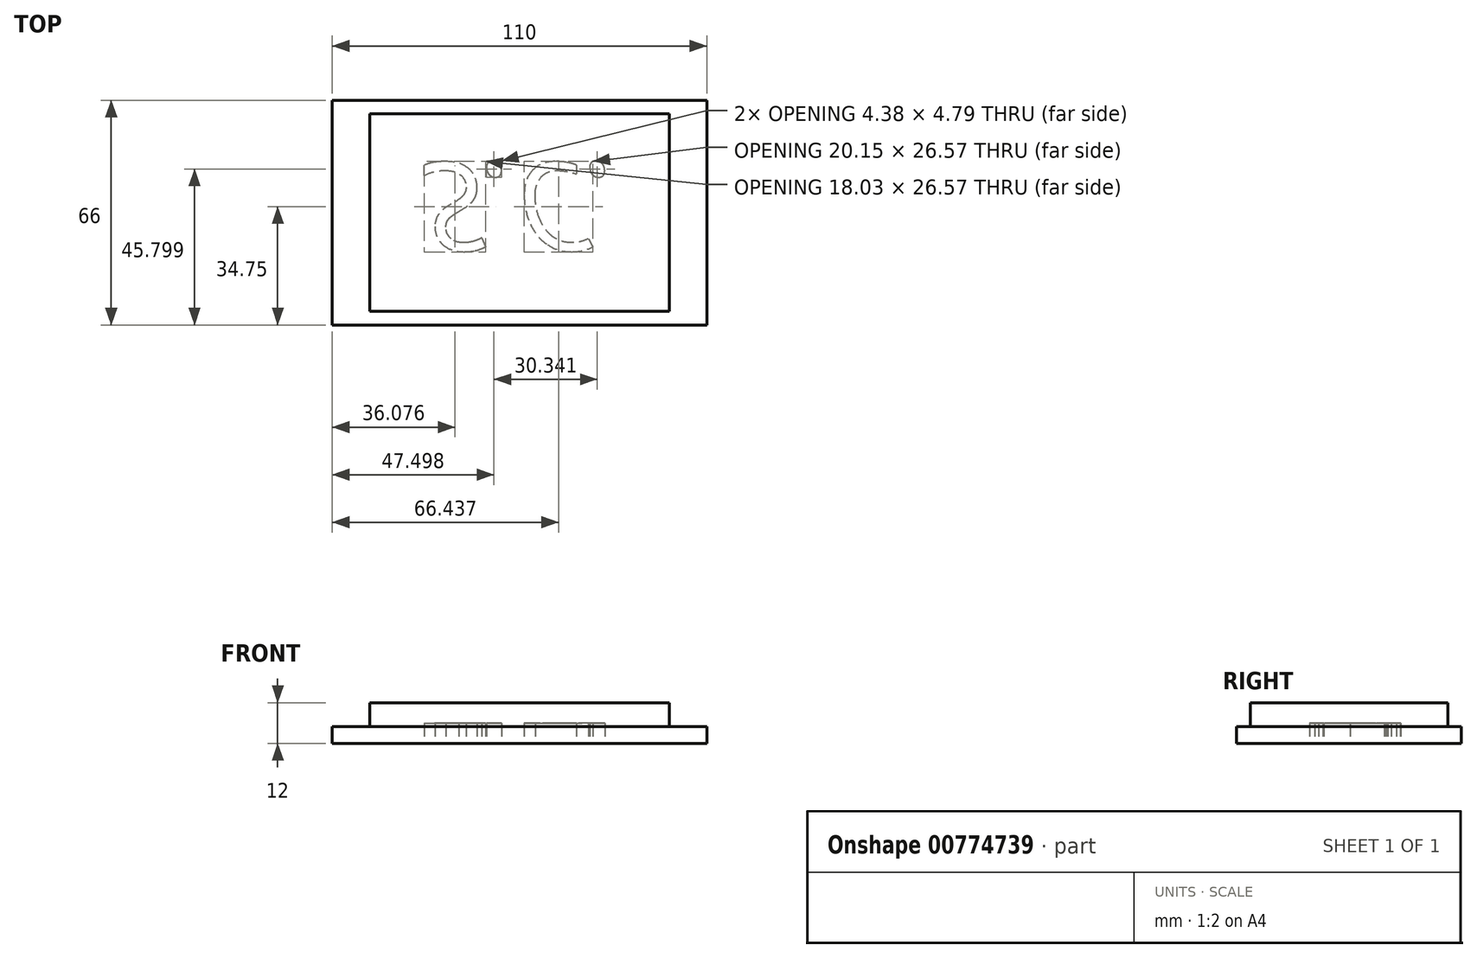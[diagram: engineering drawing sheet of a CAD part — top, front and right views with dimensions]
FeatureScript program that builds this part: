
annotation { "Feature Type Name" : "Feature", "Feature Type Description" : "" }
export const myFeature = defineFeature(function(context is Context, id is Id, definition is map)
    precondition{}
    {
        {
            var Q0;
            Q0=qCreatedBy(makeId("Top.planeOp"),FACE);
            var sketch = newSketch(context, id + "F0", { "sketchPlane" : qUnion([Q0])});
            skLineSegment(sketch, "E0.bottom", {"start": v(55, -33) * mm, "end": v(-55, -33) * mm});
            skLineSegment(sketch, "E0.top", {"start": v(55, 33) * mm, "end": v(-55, 33) * mm});
            skLineSegment(sketch, "E0.left", {"start": v(55, -33) * mm, "end": v(55, 33) * mm});
            skLineSegment(sketch, "E0.right", {"start": v(-55, -33) * mm, "end": v(-55, 33) * mm});
            skPoint(sketch, "E0.middle", {"position": v(0, 0) * mm});
            skSolve(sketch);
        }
        {
            var Q0;
            Q0=makeQuery(id+"F0.imprint","IMPRINT",FACE,{"disambiguationData":[TD([[makeQuery(id+"F0.imprint","IMPRINT",EDGE,{"derivedFrom":sQuery(id+"F0.wireOp",EDGE,"E0.bottom")}),-1.0]])]});
            extrude(context, id + "F1", {"entities" : qUnion([Q0]), "depth" : 5 * mm, "offsetDistance" : 25 * mm});
        }
        {
            var Q0;
            Q0=makeQuery(id+"F1.opExtrude","CAP_FACE",FACE,{"disambiguationData":[OSD([sQuery(id+"F0.wireOp",EDGE,"E0.bottom"),sQuery(id+"F0.wireOp",EDGE,"E0.top"),sQuery(id+"F0.wireOp",EDGE,"E0.left"),sQuery(id+"F0.wireOp",EDGE,"E0.right")])],"isStart":false});
            var sketch = newSketch(context, id + "F2", { "sketchPlane" : qUnion([Q0])});
            skLineSegment(sketch, "E1.bottom", {"start": v(44, 29) * mm, "end": v(-44, 29) * mm});
            skLineSegment(sketch, "E1.top", {"start": v(44, -29) * mm, "end": v(-44, -29) * mm});
            skLineSegment(sketch, "E1.left", {"start": v(44, 29) * mm, "end": v(44, -29) * mm});
            skLineSegment(sketch, "E1.right", {"start": v(-44, 29) * mm, "end": v(-44, -29) * mm});
            skPoint(sketch, "E1.middle", {"position": v(0, 0) * mm});
            skSolve(sketch);
        }
        {
            var Q0;
            Q0=makeQuery(id+"F2.imprint","IMPRINT",FACE,{"disambiguationData":[TD([[makeQuery(id+"F2.imprint","IMPRINT",EDGE,{"derivedFrom":sQuery(id+"F2.wireOp",EDGE,"E1.bottom")}),1.0]])]});
            extrude(context, id + "F3", {"entities" : qUnion([Q0]), "depth" : 7 * mm, "offsetDistance" : 25 * mm});
        }
        {
            var Q0;
            Q0=makeQuery(id+"F1.opExtrude","CAP_FACE",FACE,{"disambiguationData":[OSD([sQuery(id+"F0.wireOp",EDGE,"E0.bottom"),sQuery(id+"F0.wireOp",EDGE,"E0.top"),sQuery(id+"F0.wireOp",EDGE,"E0.left"),sQuery(id+"F0.wireOp",EDGE,"E0.right")])],"isStart":true});
            var sketch = newSketch(context, id + "F4", { "sketchPlane" : qUnion([Q0])});
            skText(sketch, "E2", { "text": "S.C.", "fontName": "OpenSans-Italic.ttf"});
            const initialGuessF4  = {"E2": [-0.02863, -0.01468, 1, 0, 0.02607]};
            skSetInitialGuess(sketch, initialGuessF4);
            skSolve(sketch);
        }
        {
            var Q0;
            Q0 = qSketchRegion(id + "F4", true);
            extrude(context, id + "F5", {"entities" : qUnion([Q0]), "operationType" : NewBodyOperationType.REMOVE, "oppositeDirection" : true, "depth" : 6 * mm, "offsetDistance" : 25 * mm});
        }
    });
